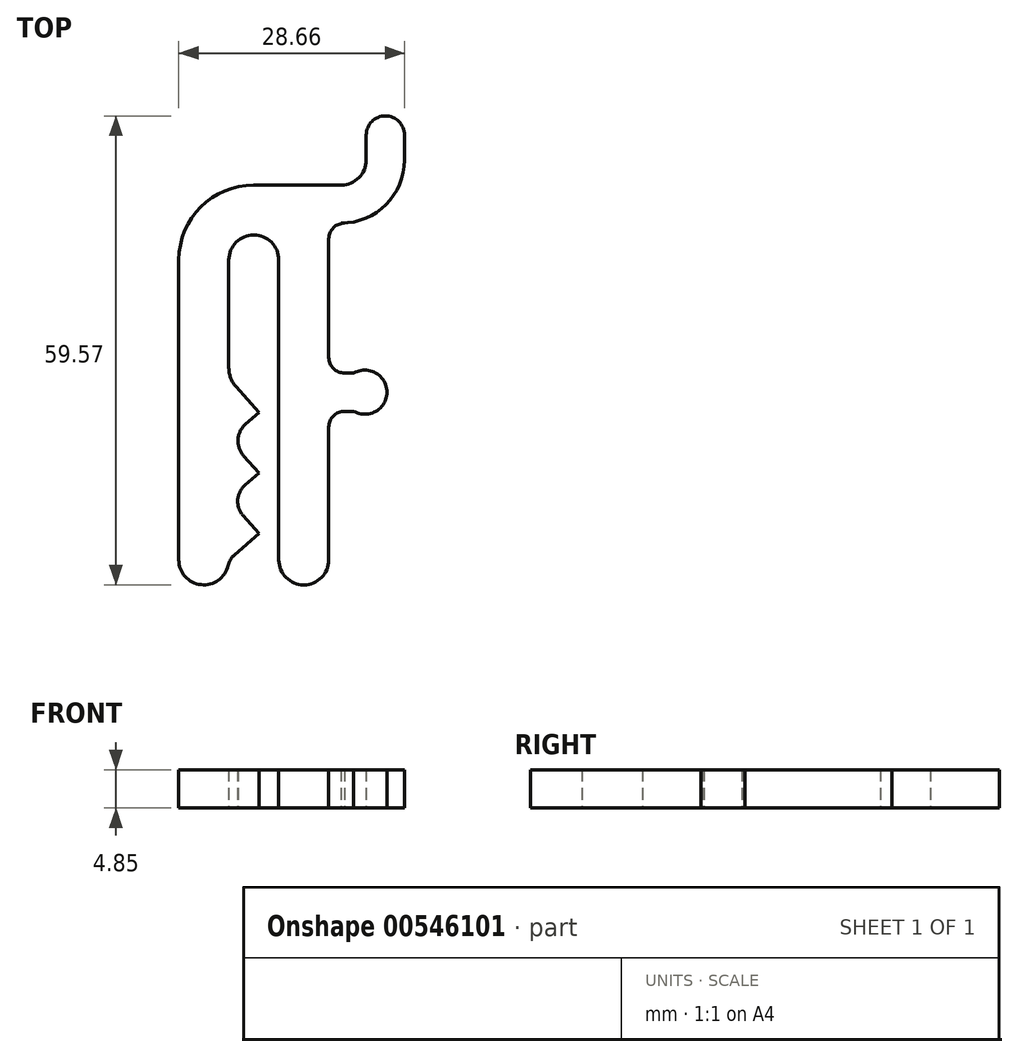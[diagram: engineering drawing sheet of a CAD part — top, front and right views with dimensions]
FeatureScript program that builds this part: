
annotation { "Feature Type Name" : "Feature", "Feature Type Description" : "" }
export const myFeature = defineFeature(function(context is Context, id is Id, definition is map)
    precondition{}
    {
        {
            assignVariable(context, id + "F0", {"name" : "tolerance", "anyValue" : 1.5 * mm});
        }
        {
            assignVariable(context, id + "F1", {"name" : "hole", "anyValue" : 6.35 * mm});
        }
        {
            var Q0;
            Q0=qCreatedBy(makeId("Top.planeOp"),FACE);
            var sketch = newSketch(context, id + "F2", { "sketchPlane" : qUnion([Q0])});
            skLineSegment(sketch, "E0", {"start": v(-3.18, 24.9) * mm, "end": v(7.94, 24.9) * mm});
            skArc(sketch, "E1", {"start": v(7.94, 24.9) * mm, "mid": v(10.18, 25.84) * mm, "end": v(11.11, 28.08) * mm});
            skArc(sketch, "E2", {"start": v(7.94, 20.06) * mm, "mid": v(13.61, 22.4) * mm, "end": v(15.96, 28.08) * mm});
            skLineSegment(sketch, "E3", {"start": v(8.35, 20.06) * mm, "end": v(7.94, 20.06) * mm});
            skLineSegment(sketch, "E4", {"start": v(6.35, 18.06) * mm, "end": v(6.35, 3) * mm});
            skLineSegment(sketch, "E5", {"start": v(8.35, 1) * mm, "end": v(9.53, 1) * mm});
            skArc(sketch, "E6", {"start": v(9.53, -3.84) * mm, "mid": v(13.72, -1.42) * mm, "end": v(9.53, 1) * mm});
            skLineSegment(sketch, "E7", {"start": v(9.53, -3.84) * mm, "end": v(8.35, -3.84) * mm});
            skLineSegment(sketch, "E8", {"start": v(6.35, -5.84) * mm, "end": v(6.35, -22.72) * mm});
            skPoint(sketch, "E9.visualSharp", {"position": v(6.35, 20.06) * mm});
            skArc(sketch, "E9.filletArc", {"start": v(8.35, 20.06) * mm, "mid": v(6.94, 19.47) * mm, "end": v(6.35, 18.06) * mm});
            skPoint(sketch, "E10.visualSharp", {"position": v(6.35, 1) * mm});
            skArc(sketch, "E10.filletArc", {"start": v(6.35, 3) * mm, "mid": v(6.94, 1.6) * mm, "end": v(8.35, 1) * mm});
            skPoint(sketch, "E11.visualSharp", {"position": v(6.35, -3.84) * mm});
            skArc(sketch, "E11.filletArc", {"start": v(8.35, -3.84) * mm, "mid": v(6.94, -4.43) * mm, "end": v(6.35, -5.84) * mm});
            skLineSegment(sketch, "E12", {"start": v(11.11, 28.08) * mm, "end": v(11.11, 31.26) * mm});
            skLineSegment(sketch, "E13", {"start": v(15.96, 28.08) * mm, "end": v(15.96, 31.26) * mm});
            skArc(sketch, "E14", {"start": v(15.96, 31.26) * mm, "mid": v(13.54, 33.68) * mm, "end": v(11.11, 31.26) * mm});
            skLineSegment(sketch, "E15", {"start": v(-12.7, 15.38) * mm, "end": v(-12.7, -22.72) * mm});
            skLineSegment(sketch, "E16", {"start": v(0, -22.72) * mm, "end": v(0, 15.38) * mm});
            skArc(sketch, "E17", {"start": v(0, -22.72) * mm, "mid": v(3.18, -25.9) * mm, "end": v(6.35, -22.72) * mm});
            skArc(sketch, "E18", {"start": v(-12.7, -22.72) * mm, "mid": v(-9.88, -25.87) * mm, "end": v(-6.43, -23.42) * mm});
            skLineSegment(sketch, "E19", {"start": v(-5.64, -22.09) * mm, "end": v(-2.54, -19.35) * mm});
            skLineSegment(sketch, "E20", {"start": v(-2.54, -19.35) * mm, "end": v(-4.55, -17.08) * mm});
            skLineSegment(sketch, "E21", {"start": v(-4.3, -13.24) * mm, "end": v(-2.54, -11.67) * mm});
            skLineSegment(sketch, "E22", {"start": v(-2.54, -11.67) * mm, "end": v(-4.47, -9.5) * mm});
            skLineSegment(sketch, "E23", {"start": v(-4.22, -5.48) * mm, "end": v(-2.54, -4) * mm});
            skLineSegment(sketch, "E24", {"start": v(-2.54, -4) * mm, "end": v(-5.45, -0.7) * mm});
            skLineSegment(sketch, "E25", {"start": v(-6.35, 1.67) * mm, "end": v(-6.35, 15.38) * mm});
            skPoint(sketch, "E26.visualSharp", {"position": v(-6.35, -15.04) * mm});
            skArc(sketch, "E26.filletArc", {"start": v(-4.3, -13.24) * mm, "mid": v(-5.22, -15.1) * mm, "end": v(-4.55, -17.08) * mm});
            skPoint(sketch, "E27.visualSharp", {"position": v(-6.35, -7.36) * mm});
            skArc(sketch, "E27.filletArc", {"start": v(-4.22, -5.48) * mm, "mid": v(-5.17, -7.43) * mm, "end": v(-4.47, -9.5) * mm});
            skPoint(sketch, "E28.visualSharp", {"position": v(-6.35, 0.31) * mm});
            skArc(sketch, "E28.filletArc", {"start": v(-6.35, 1.67) * mm, "mid": v(-6.12, 0.4) * mm, "end": v(-5.45, -0.7) * mm});
            skPoint(sketch, "E29.visualSharp", {"position": v(-6.35, -22.72) * mm});
            skArc(sketch, "E29.filletArc", {"start": v(-5.64, -22.09) * mm, "mid": v(-6.14, -22.7) * mm, "end": v(-6.43, -23.42) * mm});
            skArc(sketch, "E30", {"start": v(-3.18, 24.9) * mm, "mid": v(-9.91, 22.12) * mm, "end": v(-12.7, 15.38) * mm});
            skArc(sketch, "E31", {"start": v(0, 15.38) * mm, "mid": v(-3.17, 18.56) * mm, "end": v(-6.35, 15.38) * mm});
            skSolve(sketch);
        }
        {
            var Q0;
            Q0 = qSketchRegion(id + "F2", true);
            extrude(context, id + "F3", {"entities" : qUnion([Q0]), "depth" : getVariable(context, 'hole') - getVariable(context, 'tolerance'), "offsetDistance" : 25.4 * mm});
        }
    });
